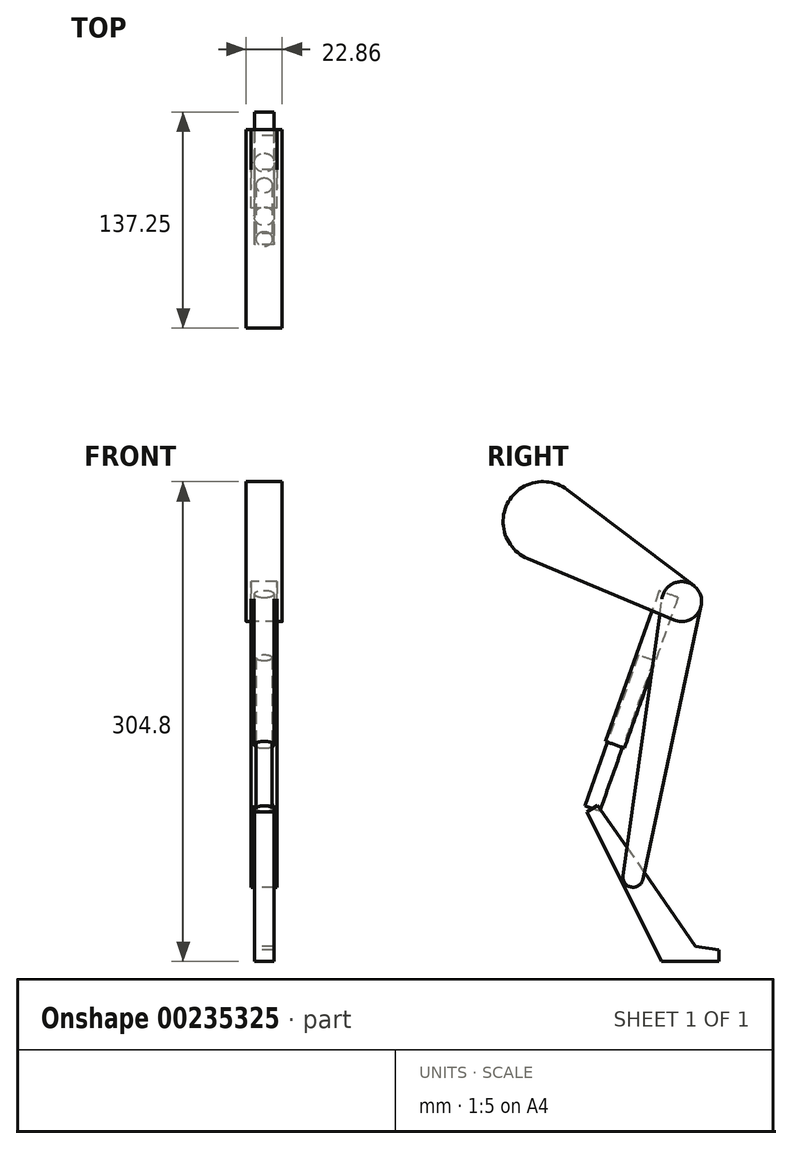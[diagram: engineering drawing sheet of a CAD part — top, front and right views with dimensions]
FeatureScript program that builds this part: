
annotation { "Feature Type Name" : "Feature", "Feature Type Description" : "" }
export const myFeature = defineFeature(function(context is Context, id is Id, definition is map)
    precondition{}
    {
        {
            var Q0;
            Q0=qCreatedBy(makeId("Right.planeOp"),FACE);
            var sketch = newSketch(context, id + "F0", { "sketchPlane" : qUnion([Q0])});
            skCircle(sketch, "E0", {"center": v(-87.99, 50.8) * mm, "radius": 25.4 * mm});
            skCircle(sketch, "E1", {"center": v(0, 0) * mm, "radius": 12.7 * mm});
            skLineSegment(sketch, "E2", {"start": v(-87.99, 50.8) * mm, "end": v(0, 0) * mm});
            skLineSegment(sketch, "E3", {"start": v(0, 0) * mm, "end": v(-30.87, -175.1) * mm});
            skLineSegment(sketch, "E4", {"start": v(-30.87, -175.1) * mm, "end": v(0, -228.6) * mm});
            skCircle(sketch, "E5", {"center": v(-30.87, -175.1) * mm, "radius": 6.35 * mm});
            skLineSegment(sketch, "E6", {"start": v(-66.74, -228.6) * mm, "end": v(112.97, -228.6) * mm, "construction": true});
            skLineSegment(sketch, "E7", {"start": v(-30.87, -175.1) * mm, "end": v(-56.77, -131.4) * mm});
            skLineSegment(sketch, "E8", {"start": v(-56.77, -131.4) * mm, "end": v(-8.27, 4.78) * mm, "construction": true});
            skLineSegment(sketch, "E9", {"start": v(-72.64, 71.04) * mm, "end": v(7.68, 10.12) * mm});
            skLineSegment(sketch, "E10", {"start": v(-97.84, 27.39) * mm, "end": v(-4.93, -11.7) * mm});
            skLineSegment(sketch, "E11", {"start": v(-37.16, -174.22) * mm, "end": v(-12.58, 1.76) * mm});
            skLineSegment(sketch, "E12", {"start": v(12.42, -2.65) * mm, "end": v(-24.66, -176.42) * mm});
            skLineSegment(sketch, "E13", {"start": v(-56.77, -131.4) * mm, "end": v(-53.33, -129.36) * mm});
            skLineSegment(sketch, "E14", {"start": v(-53.33, -129.36) * mm, "end": v(8.86, -218.97) * mm});
            skLineSegment(sketch, "E15", {"start": v(8.86, -218.97) * mm, "end": v(23.86, -221.06) * mm});
            skLineSegment(sketch, "E16", {"start": v(23.86, -221.06) * mm, "end": v(23.86, -228.6) * mm});
            skLineSegment(sketch, "E17", {"start": v(23.86, -228.6) * mm, "end": v(-12.7, -228.6) * mm});
            skLineSegment(sketch, "E18", {"start": v(-12.7, -228.6) * mm, "end": v(-60.2, -133.43) * mm});
            skLineSegment(sketch, "E19", {"start": v(-60.2, -133.43) * mm, "end": v(-56.77, -131.4) * mm});
            skSolve(sketch);
        }
        {
            var Q0;
            Q0=makeQuery(id+"F0.imprint","IMPRINT",FACE,{"disambiguationData":[TD([[makeQuery(id+"F0.imprint","IMPRINT",EDGE,{"derivedFrom":sQuery(id+"F0.wireOp",EDGE,"E0")}),1.0]])]});
            var Q1;
            {var subQ0=sQuery(id+"F0.wireOp",EDGE,"E9");Q1=makeQuery(id+"F0.imprint","IMPRINT",FACE,{"disambiguationData":[TD([[makeQuery(id+"F0.imprint","IMPRINT",EDGE,{"derivedFrom":subQ0}),-1.0]])]});}
            var Q2;
            {var subQ0=sQuery(id+"F0.wireOp",EDGE,"E10");var subQ1=sQuery(id+"F0.wireOp",EDGE,"E0");var subQ2=makeQuery(id+"F0.imprint","INTERSECT",VERTEX,{"derivedFrom":[subQ1,subQ0]});Q2=makeQuery(id+"F0.imprint","IMPRINT",FACE,{"disambiguationData":[TD([[makeQuery(id+"F0.imprint","IMPRINT",EDGE,{"disambiguationData":[TD([[subQ2,-1.0]])],"derivedFrom":subQ1}),-1.0]])]});}
            var Q3;
            {var subQ0=sQuery(id+"F0.wireOp",EDGE,"E10");var subQ1=sQuery(id+"F0.wireOp",EDGE,"E1");var subQ2=makeQuery(id+"F0.imprint","INTERSECT",VERTEX,{"derivedFrom":[subQ1,subQ0]});Q3=makeQuery(id+"F0.imprint","IMPRINT",FACE,{"disambiguationData":[TD([[makeQuery(id+"F0.imprint","IMPRINT",EDGE,{"disambiguationData":[TD([[subQ2,1.0]])],"derivedFrom":subQ1}),-1.0]])]});}
            var Q4;
            {var subQ3=sQuery(id+"F0.wireOp",EDGE,"E1");var subQ7=makeQuery(id+"F0.imprint","INTERSECT",VERTEX,{"derivedFrom":[subQ3,sQuery(id+"F0.wireOp",EDGE,"E11")]});Q4=makeQuery(id+"F0.imprint","IMPRINT",FACE,{"disambiguationData":[TD([[makeQuery(id+"F0.imprint","IMPRINT",EDGE,{"disambiguationData":[TD([[subQ7,1.0]])],"derivedFrom":subQ3}),1.0]])]});}
            var Q5;
            {var subQ3=sQuery(id+"F0.wireOp",EDGE,"E1");var subQ5=makeQuery(id+"F0.imprint","INTERSECT",VERTEX,{"derivedFrom":[subQ3,sQuery(id+"F0.wireOp",EDGE,"E9")]});Q5=makeQuery(id+"F0.imprint","IMPRINT",FACE,{"disambiguationData":[TD([[makeQuery(id+"F0.imprint","IMPRINT",EDGE,{"disambiguationData":[TD([[subQ5,-1.0]])],"derivedFrom":subQ3}),1.0]])]});}
            extrude(context, id + "F1", {"entities" : qUnion([Q0, Q1, Q2, Q3, Q4, Q5]), "endBound" : BoundingType.SYMMETRIC, "depth" : 22.86 * mm});
        }
        {
            var Q0;
            {var subQ0=sQuery(id+"F0.wireOp",EDGE,"E2");var subQ1=sQuery(id+"F0.wireOp",EDGE,"E1");var subQ2=makeQuery(id+"F0.imprint","INTERSECT",VERTEX,{"derivedFrom":[subQ1,subQ0]});Q0=makeQuery(id+"F0.imprint","IMPRINT",FACE,{"disambiguationData":[TD([[makeQuery(id+"F0.imprint","IMPRINT",EDGE,{"disambiguationData":[TD([[subQ2,1.0]])],"derivedFrom":subQ1}),1.0]])]});}
            var Q1;
            {var subQ0=sQuery(id+"F0.wireOp",EDGE,"E2");var subQ1=sQuery(id+"F0.wireOp",EDGE,"E1");var subQ2=makeQuery(id+"F0.imprint","INTERSECT",VERTEX,{"derivedFrom":[subQ1,subQ0]});Q1=makeQuery(id+"F0.imprint","IMPRINT",FACE,{"disambiguationData":[TD([[makeQuery(id+"F0.imprint","IMPRINT",EDGE,{"disambiguationData":[TD([[subQ2,-1.0]])],"derivedFrom":subQ1}),1.0]])]});}
            var Q2;
            {var subQ4=sQuery(id+"F0.wireOp",EDGE,"E12");var subQ5=sQuery(id+"F0.wireOp",EDGE,"E1");var subQ6=makeQuery(id+"F0.imprint","INTERSECT",VERTEX,{"derivedFrom":[subQ5,subQ4]});Q2=makeQuery(id+"F0.imprint","IMPRINT",FACE,{"disambiguationData":[TD([[makeQuery(id+"F0.imprint","IMPRINT",EDGE,{"disambiguationData":[TD([[subQ6,1.0]])],"derivedFrom":subQ5}),-1.0]])]});}
            var Q3;
            {var subQ1=sQuery(id+"F0.wireOp",EDGE,"E10");var subQ5=sQuery(id+"F0.wireOp",EDGE,"E1");var subQ6=makeQuery(id+"F0.imprint","INTERSECT",VERTEX,{"derivedFrom":[subQ5,subQ1]});Q3=makeQuery(id+"F0.imprint","IMPRINT",FACE,{"disambiguationData":[TD([[makeQuery(id+"F0.imprint","IMPRINT",EDGE,{"disambiguationData":[TD([[subQ6,-1.0]])],"derivedFrom":subQ5}),-1.0]])]});}
            var Q4;
            {var subQ0=sQuery(id+"F0.wireOp",EDGE,"E10");var subQ1=sQuery(id+"F0.wireOp",EDGE,"E1");var subQ2=makeQuery(id+"F0.imprint","INTERSECT",VERTEX,{"derivedFrom":[subQ1,subQ0]});Q4=makeQuery(id+"F0.imprint","IMPRINT",FACE,{"disambiguationData":[TD([[makeQuery(id+"F0.imprint","IMPRINT",EDGE,{"disambiguationData":[TD([[subQ2,1.0]])],"derivedFrom":subQ1}),-1.0]])]});}
            var Q5;
            {var subQ0=sQuery(id+"F0.wireOp",EDGE,"E5");var subQ4=makeQuery(id+"F0.imprint","INTERSECT",VERTEX,{"derivedFrom":[subQ0,sQuery(id+"F0.wireOp",EDGE,"E11")]});Q5=makeQuery(id+"F0.imprint","IMPRINT",FACE,{"disambiguationData":[TD([[makeQuery(id+"F0.imprint","IMPRINT",EDGE,{"disambiguationData":[TD([[subQ4,1.0]])],"derivedFrom":subQ0}),1.0]])]});}
            var Q6;
            {var subQ0=sQuery(id+"F0.wireOp",EDGE,"E14");var subQ5=sQuery(id+"F0.wireOp",EDGE,"E3");var subQ6=makeQuery(id+"F0.imprint","INTERSECT",VERTEX,{"derivedFrom":[subQ5,subQ0]});Q6=makeQuery(id+"F0.imprint","IMPRINT",FACE,{"disambiguationData":[TD([[makeQuery(id+"F0.imprint","IMPRINT",EDGE,{"disambiguationData":[TD([[subQ6,-1.0]])],"derivedFrom":subQ5}),-1.0]])]});}
            var Q7;
            {var subQ0=sQuery(id+"F0.wireOp",EDGE,"E11");var subQ1=sQuery(id+"F0.wireOp",EDGE,"E5");var subQ2=makeQuery(id+"F0.imprint","INTERSECT",VERTEX,{"derivedFrom":[subQ1,subQ0]});Q7=makeQuery(id+"F0.imprint","IMPRINT",FACE,{"disambiguationData":[TD([[makeQuery(id+"F0.imprint","IMPRINT",EDGE,{"disambiguationData":[TD([[subQ2,1.0]])],"derivedFrom":subQ1}),-1.0]])]});}
            var Q8;
            {var subQ0=sQuery(id+"F0.wireOp",EDGE,"E14");var subQ1=sQuery(id+"F0.wireOp",EDGE,"E3");var subQ2=makeQuery(id+"F0.imprint","INTERSECT",VERTEX,{"derivedFrom":[subQ1,subQ0]});Q8=makeQuery(id+"F0.imprint","IMPRINT",FACE,{"disambiguationData":[TD([[makeQuery(id+"F0.imprint","IMPRINT",EDGE,{"disambiguationData":[TD([[subQ2,-1.0]])],"derivedFrom":subQ1}),1.0]])]});}
            var Q9;
            {var subQ0=sQuery(id+"F0.wireOp",EDGE,"E5");var subQ5=sQuery(id+"F0.wireOp",EDGE,"E3");var subQ6=makeQuery(id+"F0.imprint","INTERSECT",VERTEX,{"derivedFrom":[subQ5,subQ0]});Q9=makeQuery(id+"F0.imprint","IMPRINT",FACE,{"disambiguationData":[TD([[makeQuery(id+"F0.imprint","IMPRINT",EDGE,{"disambiguationData":[TD([[subQ6,1.0]])],"derivedFrom":subQ0}),1.0]])]});}
            var Q10;
            {var subQ1=sQuery(id+"F0.wireOp",EDGE,"E3");var subQ3=sQuery(id+"F0.wireOp",EDGE,"E5");var subQ4=makeQuery(id+"F0.imprint","INTERSECT",VERTEX,{"derivedFrom":[subQ1,subQ3]});Q10=makeQuery(id+"F0.imprint","IMPRINT",FACE,{"disambiguationData":[TD([[makeQuery(id+"F0.imprint","IMPRINT",EDGE,{"disambiguationData":[TD([[subQ4,-1.0]])],"derivedFrom":subQ3}),1.0]])]});}
            var Q11;
            {var subQ0=sQuery(id+"F0.wireOp",EDGE,"E12");var subQ1=sQuery(id+"F0.wireOp",EDGE,"E5");var subQ2=makeQuery(id+"F0.imprint","INTERSECT",VERTEX,{"derivedFrom":[subQ1,subQ0]});Q11=makeQuery(id+"F0.imprint","IMPRINT",FACE,{"disambiguationData":[TD([[makeQuery(id+"F0.imprint","IMPRINT",EDGE,{"disambiguationData":[TD([[subQ2,-1.0]])],"derivedFrom":subQ1}),-1.0]])]});}
            extrude(context, id + "F2", {"entities" : qUnion([Q0, Q1, Q2, Q3, Q4, Q5, Q6, Q7, Q8, Q9, Q10, Q11]), "endBound" : BoundingType.SYMMETRIC, "depth" : 16.5 * mm});
        }
        {
            var Q0;
            {var subQ10=sQuery(id+"F0.wireOp",EDGE,"E18");Q0=makeQuery(id+"F0.imprint","IMPRINT",FACE,{"disambiguationData":[TD([[makeQuery(id+"F0.imprint","IMPRINT",EDGE,{"derivedFrom":subQ10}),-1.0]])]});}
            var Q1;
            {var subQ0=sQuery(id+"F0.wireOp",EDGE,"E13");Q1=makeQuery(id+"F0.imprint","IMPRINT",FACE,{"disambiguationData":[TD([[makeQuery(id+"F0.imprint","IMPRINT",EDGE,{"derivedFrom":subQ0}),-1.0]])]});}
            var Q2;
            {var subQ5=sQuery(id+"F0.wireOp",EDGE,"E14");var subQ7=sQuery(id+"F0.wireOp",EDGE,"E3");var subQ9=makeQuery(id+"F0.imprint","INTERSECT",VERTEX,{"derivedFrom":[subQ7,subQ5]});Q2=makeQuery(id+"F0.imprint","IMPRINT",FACE,{"disambiguationData":[TD([[makeQuery(id+"F0.imprint","IMPRINT",EDGE,{"disambiguationData":[TD([[subQ9,-1.0]])],"derivedFrom":subQ7}),-1.0]])]});}
            var Q3;
            {var subQ0=sQuery(id+"F0.wireOp",EDGE,"E11");var subQ1=sQuery(id+"F0.wireOp",EDGE,"E5");var subQ2=makeQuery(id+"F0.imprint","INTERSECT",VERTEX,{"derivedFrom":[subQ1,subQ0]});Q3=makeQuery(id+"F0.imprint","IMPRINT",FACE,{"disambiguationData":[TD([[makeQuery(id+"F0.imprint","IMPRINT",EDGE,{"disambiguationData":[TD([[subQ2,1.0]])],"derivedFrom":subQ1}),-1.0]])]});}
            var Q4;
            {var subQ3=sQuery(id+"F0.wireOp",EDGE,"E5");var subQ5=makeQuery(id+"F0.imprint","INTERSECT",VERTEX,{"derivedFrom":[subQ3,sQuery(id+"F0.wireOp",EDGE,"E11")]});Q4=makeQuery(id+"F0.imprint","IMPRINT",FACE,{"disambiguationData":[TD([[makeQuery(id+"F0.imprint","IMPRINT",EDGE,{"disambiguationData":[TD([[subQ5,1.0]])],"derivedFrom":subQ3}),1.0]])]});}
            var Q5;
            {var subQ1=sQuery(id+"F0.wireOp",EDGE,"E3");var subQ3=sQuery(id+"F0.wireOp",EDGE,"E5");var subQ4=makeQuery(id+"F0.imprint","INTERSECT",VERTEX,{"derivedFrom":[subQ1,subQ3]});Q5=makeQuery(id+"F0.imprint","IMPRINT",FACE,{"disambiguationData":[TD([[makeQuery(id+"F0.imprint","IMPRINT",EDGE,{"disambiguationData":[TD([[subQ4,-1.0]])],"derivedFrom":subQ3}),1.0]])]});}
            var Q6;
            {var subQ0=sQuery(id+"F0.wireOp",EDGE,"E14");var subQ1=sQuery(id+"F0.wireOp",EDGE,"E3");var subQ2=makeQuery(id+"F0.imprint","INTERSECT",VERTEX,{"derivedFrom":[subQ1,subQ0]});Q6=makeQuery(id+"F0.imprint","IMPRINT",FACE,{"disambiguationData":[TD([[makeQuery(id+"F0.imprint","IMPRINT",EDGE,{"disambiguationData":[TD([[subQ2,-1.0]])],"derivedFrom":subQ1}),1.0]])]});}
            var Q7;
            {var subQ3=sQuery(id+"F0.wireOp",EDGE,"E5");var subQ6=makeQuery(id+"F0.imprint","INTERSECT",VERTEX,{"derivedFrom":[subQ3,sQuery(id+"F0.wireOp",EDGE,"E12")]});Q7=makeQuery(id+"F0.imprint","IMPRINT",FACE,{"disambiguationData":[TD([[makeQuery(id+"F0.imprint","IMPRINT",EDGE,{"disambiguationData":[TD([[subQ6,1.0]])],"derivedFrom":subQ3}),1.0]])]});}
            var Q8;
            {var subQ5=sQuery(id+"F0.wireOp",EDGE,"E15");Q8=makeQuery(id+"F0.imprint","IMPRINT",FACE,{"disambiguationData":[TD([[makeQuery(id+"F0.imprint","IMPRINT",EDGE,{"derivedFrom":subQ5}),-1.0]])]});}
            extrude(context, id + "F3", {"entities" : qUnion([Q0, Q1, Q2, Q3, Q4, Q5, Q6, Q7, Q8]), "endBound" : BoundingType.SYMMETRIC, "depth" : 12.2 * mm});
        }
        {
            var Q0;
            Q0=qCreatedBy(makeId("Right.planeOp"),FACE);
            var sketch = newSketch(context, id + "F4", { "sketchPlane" : qUnion([Q0])});
            skLineSegment(sketch, "E20.bottom", {"start": v(-56.77, -131.4) * mm, "end": v(-61.55, -129.69) * mm});
            skLineSegment(sketch, "E20.top", {"start": v(-22.68, -35.68) * mm, "end": v(-27.47, -33.98) * mm});
            skLineSegment(sketch, "E20.left", {"start": v(-56.77, -131.4) * mm, "end": v(-22.68, -35.68) * mm});
            skLineSegment(sketch, "E20.right", {"start": v(-61.55, -129.69) * mm, "end": v(-27.47, -33.98) * mm});
            skLineSegment(sketch, "E21.bottom", {"start": v(-42.36, -90.94) * mm, "end": v(-48.34, -88.8) * mm});
            skLineSegment(sketch, "E21.top", {"start": v(-8.27, 4.78) * mm, "end": v(-14.25, 6.9) * mm});
            skLineSegment(sketch, "E21.left", {"start": v(-42.36, -90.94) * mm, "end": v(-8.27, 4.78) * mm});
            skLineSegment(sketch, "E21.right", {"start": v(-48.34, -88.8) * mm, "end": v(-14.25, 6.9) * mm});
            skSolve(sketch);
        }
        {
            var Q0;
            {var subQ5=sQuery(id+"F4.wireOp",EDGE,"E20.top");Q0=makeQuery(id+"F4.imprint","IMPRINT",FACE,{"disambiguationData":[TD([[makeQuery(id+"F4.imprint","IMPRINT",EDGE,{"derivedFrom":subQ5}),-1.0]])]});}
            var Q1;
            {var subQ0=sQuery(id+"F4.wireOp",EDGE,"E20.top");Q1=makeQuery(id+"F4.imprint","IMPRINT",FACE,{"disambiguationData":[TD([[makeQuery(id+"F4.imprint","IMPRINT",EDGE,{"derivedFrom":subQ0}),1.0]])]});}
            var Q2;
            Q2=sQuery(id+"F4.wireOp",EDGE,"E21.left");
            revolve(context, id + "F5", {"entities" : qUnion([Q0, Q1]), "axis" : qUnion([Q2]), "revolveType" : RevolveType.FULL});
        }
        {
            var Q0;
            {var subQ0=sQuery(id+"F4.wireOp",EDGE,"E20.top");Q0=makeQuery(id+"F4.imprint","IMPRINT",FACE,{"disambiguationData":[TD([[makeQuery(id+"F4.imprint","IMPRINT",EDGE,{"derivedFrom":subQ0}),1.0]])]});}
            var Q1;
            {var subQ0=sQuery(id+"F4.wireOp",EDGE,"E20.bottom");Q1=makeQuery(id+"F4.imprint","IMPRINT",FACE,{"disambiguationData":[TD([[makeQuery(id+"F4.imprint","IMPRINT",EDGE,{"derivedFrom":subQ0}),-1.0]])]});}
            var Q2;
            Q2=sQuery(id+"F4.wireOp",EDGE,"E20.left");
            revolve(context, id + "F6", {"entities" : qUnion([Q0, Q1]), "axis" : qUnion([Q2]), "revolveType" : RevolveType.FULL});
        }
    });
